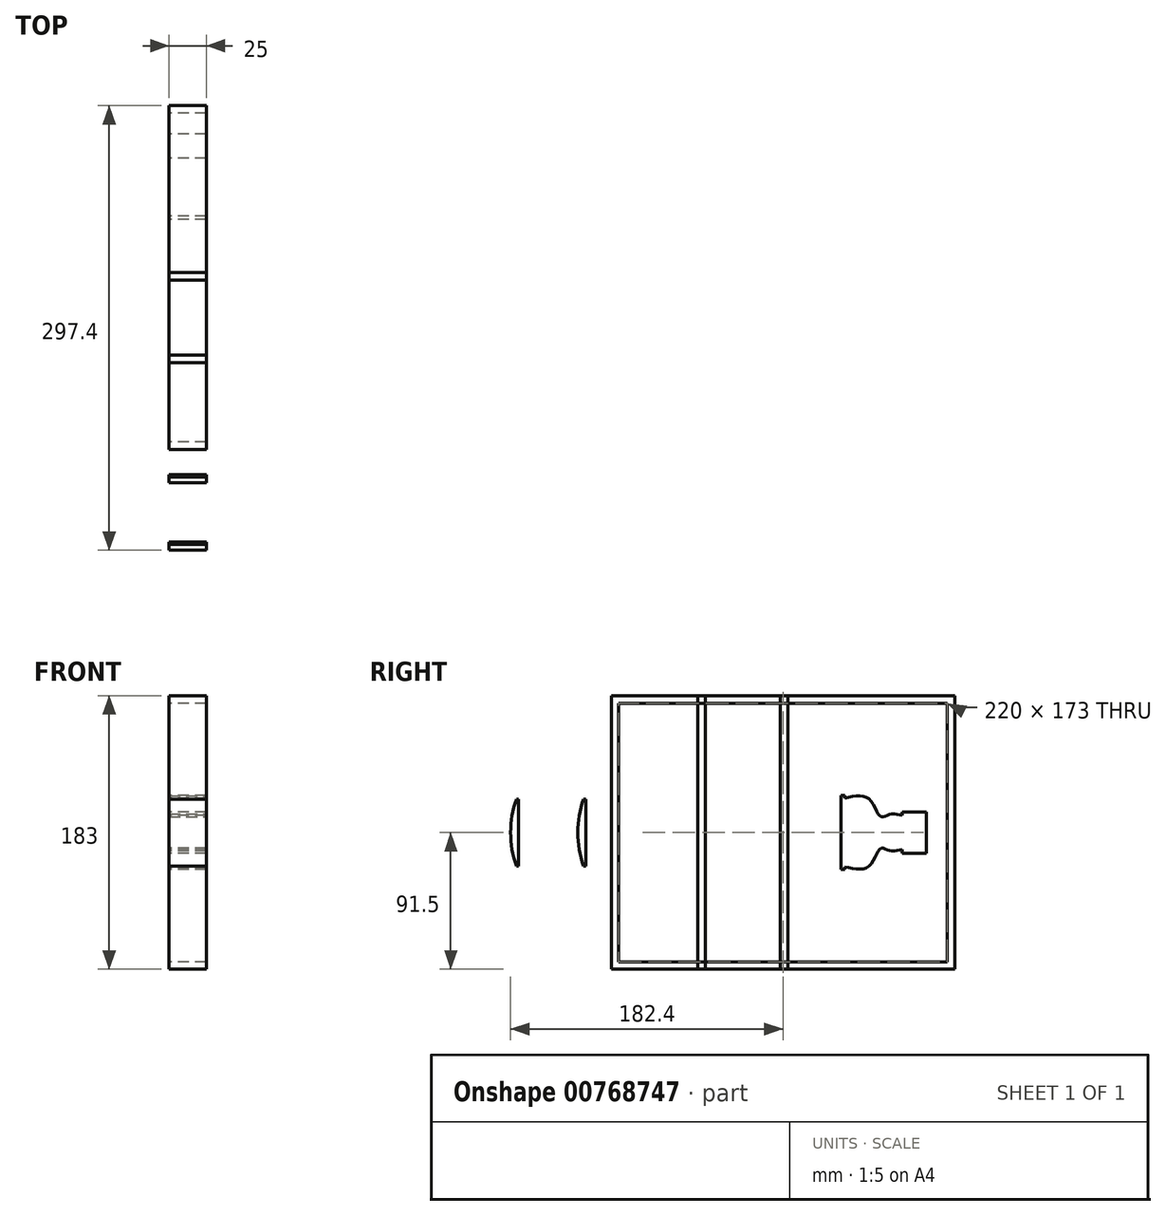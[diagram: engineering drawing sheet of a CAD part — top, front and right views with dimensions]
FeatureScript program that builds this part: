
annotation { "Feature Type Name" : "Feature", "Feature Type Description" : "" }
export const myFeature = defineFeature(function(context is Context, id is Id, definition is map)
    precondition{}
    {
        {
            var Q0;
            Q0=qCreatedBy(makeId("Right.planeOp"),FACE);
            var sketch = newSketch(context, id + "F0", { "sketchPlane" : qUnion([Q0])});
            skLineSegment(sketch, "E0", {"start": v(0, 0) * mm, "end": v(115, 0) * mm, "construction": true});
            skLineSegment(sketch, "E1.bottom", {"start": v(0, 91.5) * mm, "end": v(230, 91.5) * mm, "construction": true});
            skLineSegment(sketch, "E1.top", {"start": v(0, -91.5) * mm, "end": v(230, -91.5) * mm, "construction": true});
            skLineSegment(sketch, "E1.left", {"start": v(0, 91.5) * mm, "end": v(0, -91.5) * mm, "construction": true});
            skLineSegment(sketch, "E1.right", {"start": v(230, 91.5) * mm, "end": v(230, -91.5) * mm, "construction": true});
            skPoint(sketch, "E1.middle", {"position": v(115, 0) * mm});
            skLineSegment(sketch, "E2", {"start": v(58, 91.5) * mm, "end": v(58, -91.5) * mm, "construction": true});
            skLineSegment(sketch, "E3", {"start": v(121, -91.5) * mm, "end": v(121, 91.5) * mm, "construction": true});
            skLineSegment(sketch, "E4.0", {"start": v(65.7, 91.5) * mm, "end": v(65.7, -91.5) * mm, "construction": true});
            skLineSegment(sketch, "E5.0", {"start": v(113.3, -91.5) * mm, "end": v(113.3, 91.5) * mm, "construction": true});
            skLineSegment(sketch, "E6.bottom", {"start": v(0, 37.5) * mm, "end": v(-62, 37.5) * mm, "construction": true});
            skLineSegment(sketch, "E6.top", {"start": v(0, -37.5) * mm, "end": v(-62, -37.5) * mm, "construction": true});
            skLineSegment(sketch, "E6.right", {"start": v(-62, 37.5) * mm, "end": v(-62, -37.5) * mm, "construction": true});
            skLineSegment(sketch, "E7.0", {"start": v(11, 80.5) * mm, "end": v(219, 80.5) * mm, "construction": true});
            skLineSegment(sketch, "E7.1", {"start": v(11, 80.5) * mm, "end": v(11, -80.5) * mm, "construction": true});
            skLineSegment(sketch, "E7.2", {"start": v(11, -80.5) * mm, "end": v(219, -80.5) * mm, "construction": true});
            skLineSegment(sketch, "E7.3", {"start": v(219, 80.5) * mm, "end": v(219, -80.5) * mm, "construction": true});
            skLineSegment(sketch, "E8", {"start": v(-62, 0) * mm, "end": v(0, 0) * mm, "construction": true});
            skLineSegment(sketch, "E9", {"start": v(-17, 37.5) * mm, "end": v(-17, -37.5) * mm, "construction": true});
            skSolve(sketch);
        }
        {
            var Q0;
            Q0=qCreatedBy(makeId("Right.planeOp"),FACE);
            var sketch = newSketch(context, id + "F1", { "sketchPlane" : qUnion([Q0])});
            skLineSegment(sketch, "E10", {"start": v(153.87, 24.75) * mm, "end": v(153.87, -24.75) * mm, "construction": true});
            skLineSegment(sketch, "E11", {"start": v(0, 0) * mm, "end": v(202.87, 0) * mm, "construction": true});
            skLineSegment(sketch, "E12.bottom", {"start": v(210.87, 13.75) * mm, "end": v(194.87, 13.75) * mm, "construction": true});
            skLineSegment(sketch, "E12.top", {"start": v(210.87, -13.75) * mm, "end": v(194.87, -13.75) * mm, "construction": true});
            skLineSegment(sketch, "E12.left", {"start": v(210.87, 13.75) * mm, "end": v(210.87, -13.75) * mm, "construction": true});
            skLineSegment(sketch, "E12.right", {"start": v(194.87, 13.75) * mm, "end": v(194.87, -13.75) * mm, "construction": true});
            skPoint(sketch, "E12.middle", {"position": v(202.87, 0) * mm});
            skLineSegment(sketch, "E13.0", {"start": v(156.17, 24.75) * mm, "end": v(156.17, -24.75) * mm, "construction": true});
            skLineSegment(sketch, "E14", {"start": v(153.87, 24.75) * mm, "end": v(156.17, 24.75) * mm, "construction": true});
            skLineSegment(sketch, "E15", {"start": v(153.87, -24.75) * mm, "end": v(156.17, -24.75) * mm, "construction": true});
            skFitSpline(sketch, "E16", {"points": [v(156.17, 22.99) * mm, v(180.9, 13.2) * mm, v(194.87, 11.35) * mm], "startDerivative": vector(85.68, -3.1) * mm, "endDerivative": vector(63.31, -4.77) * mm, "construction": true});
            skFitSpline(sketch, "E17.MirrorCS", {"points": [v(156.17, -22.99) * mm, v(180.9, -13.2) * mm, v(194.87, -11.35) * mm], "startDerivative": vector(85.68, 3.1) * mm, "endDerivative": vector(63.31, 4.77) * mm, "construction": true});
            skPoint(sketch, "E18", {"position": v(156.17, 0) * mm});
            skSolve(sketch);
        }
        {
            var Q0;
            Q0=qCreatedBy(makeId("Right.planeOp"),FACE);
            var sketch = newSketch(context, id + "F2", { "sketchPlane" : qUnion([Q0])});
            skLineSegment(sketch, "E19.0", {"start": v(0, 37.5) * mm, "end": v(-62, 37.5) * mm, "construction": true});
            skLineSegment(sketch, "E19.1", {"start": v(-62, 37.5) * mm, "end": v(-62, -37.5) * mm, "construction": true});
            skLineSegment(sketch, "E19.2", {"start": v(-17, 37.5) * mm, "end": v(-17, -37.5) * mm, "construction": true});
            skLineSegment(sketch, "E19.3", {"start": v(0, -37.5) * mm, "end": v(-62, -37.5) * mm, "construction": true});
            skLineSegment(sketch, "E19.4", {"start": v(0, 91.5) * mm, "end": v(0, -91.5) * mm, "construction": true});
            skLineSegment(sketch, "E19.5", {"start": v(0, 91.5) * mm, "end": v(230, 91.5) * mm, "construction": true});
            skLineSegment(sketch, "E19.6", {"start": v(230, 91.5) * mm, "end": v(230, -91.5) * mm, "construction": true});
            skLineSegment(sketch, "E19.7", {"start": v(0, -91.5) * mm, "end": v(230, -91.5) * mm, "construction": true});
            skLineSegment(sketch, "E19.8", {"start": v(58, 91.5) * mm, "end": v(58, -91.5) * mm, "construction": true});
            skLineSegment(sketch, "E19.9", {"start": v(113.3, -91.5) * mm, "end": v(113.3, 91.5) * mm, "construction": true});
            skLineSegment(sketch, "E20.0", {"start": v(210.87, 13.75) * mm, "end": v(194.87, 13.75) * mm});
            skFitSpline(sketch, "E20.1", {"points": [v(156.17, 22.99) * mm, v(172.7, 22.39) * mm, v(180.38, 10.65) * mm, v(185.98, 12.02) * mm, v(194.87, 11.35) * mm]});
            skFitSpline(sketch, "E20.2", {"points": [v(156.17, -22.99) * mm, v(172.7, -22.39) * mm, v(180.38, -10.65) * mm, v(185.98, -12.02) * mm, v(194.87, -11.35) * mm]});
            skLineSegment(sketch, "E20.3", {"start": v(210.87, -13.75) * mm, "end": v(194.87, -13.75) * mm});
            skLineSegment(sketch, "E20.4", {"start": v(210.87, 13.75) * mm, "end": v(210.87, -13.75) * mm});
            skLineSegment(sketch, "E20.5", {"start": v(153.87, 24.75) * mm, "end": v(153.87, -24.75) * mm});
            skLineSegment(sketch, "E20.6", {"start": v(153.87, 24.75) * mm, "end": v(156.17, 24.75) * mm});
            skLineSegment(sketch, "E20.7", {"start": v(153.87, -24.75) * mm, "end": v(156.17, -24.75) * mm});
            skLineSegment(sketch, "E21", {"start": v(156.17, 22.99) * mm, "end": v(156.17, 24.75) * mm});
            skLineSegment(sketch, "E22", {"start": v(156.17, -22.99) * mm, "end": v(156.17, -24.75) * mm});
            skLineSegment(sketch, "E23", {"start": v(194.87, -13.75) * mm, "end": v(194.87, -11.35) * mm});
            skLineSegment(sketch, "E24", {"start": v(194.87, 11.35) * mm, "end": v(194.87, 13.75) * mm});
            skLineSegment(sketch, "E25.0", {"start": v(225, 86.5) * mm, "end": v(225, -86.5) * mm, "construction": true});
            skLineSegment(sketch, "E25.1", {"start": v(5, 86.5) * mm, "end": v(225, 86.5) * mm, "construction": true});
            skLineSegment(sketch, "E25.2", {"start": v(5, 86.5) * mm, "end": v(5, -86.5) * mm, "construction": true});
            skLineSegment(sketch, "E25.3", {"start": v(5, -86.5) * mm, "end": v(225, -86.5) * mm, "construction": true});
            skArc(sketch, "E26", {"start": v(-18.5, 22.37) * mm, "mid": v(-22.4, 0) * mm, "end": v(-18.5, -22.37) * mm});
            skLineSegment(sketch, "E27", {"start": v(-18.5, 22.38) * mm, "end": v(-17, 22.38) * mm});
            skLineSegment(sketch, "E28", {"start": v(-18.5, -22.38) * mm, "end": v(-17, -22.38) * mm});
            skLineSegment(sketch, "E29", {"start": v(-17, 22.38) * mm, "end": v(-17, -22.38) * mm});
            skArc(sketch, "E30.1.0.0", {"start": v(-63.5, 22.38) * mm, "mid": v(-67.4, 0) * mm, "end": v(-63.5, -22.38) * mm});
            skLineSegment(sketch, "E30.1.0.1", {"start": v(-62, 22.37) * mm, "end": v(-62, -22.37) * mm});
            skLineSegment(sketch, "E30.1.0.2", {"start": v(-63.5, -22.38) * mm, "end": v(-62, -22.38) * mm});
            skLineSegment(sketch, "E30.1.0.3", {"start": v(-63.5, 22.38) * mm, "end": v(-62, 22.38) * mm});
            skLineSegment(sketch, "E30.direction1", {"start": v(-18.5, -22.37) * mm, "end": v(-63.5, -22.37) * mm, "construction": true});
            skSolve(sketch);
        }
        {
            var Q0;
            Q0=qCreatedBy(makeId("Right.planeOp"),FACE);
            var sketch = newSketch(context, id + "F3", { "sketchPlane" : qUnion([Q0])});
            skLineSegment(sketch, "E31.0", {"start": v(5, 86.5) * mm, "end": v(5, -86.5) * mm});
            skLineSegment(sketch, "E31.1", {"start": v(0, 91.5) * mm, "end": v(0, -91.5) * mm});
            skLineSegment(sketch, "E31.2", {"start": v(5, -86.5) * mm, "end": v(225, -86.5) * mm});
            skLineSegment(sketch, "E31.3", {"start": v(0, -91.5) * mm, "end": v(230, -91.5) * mm});
            skLineSegment(sketch, "E31.4", {"start": v(5, 86.5) * mm, "end": v(225, 86.5) * mm});
            skLineSegment(sketch, "E31.5", {"start": v(0, 91.5) * mm, "end": v(230, 91.5) * mm});
            skLineSegment(sketch, "E31.6", {"start": v(225, 86.5) * mm, "end": v(225, -86.5) * mm});
            skLineSegment(sketch, "E31.7", {"start": v(230, 91.5) * mm, "end": v(230, -91.5) * mm});
            skSolve(sketch);
        }
        {
            var Q0;
            Q0 = qSketchRegion(id + "F3", true);
            extrude(context, id + "F4", {"entities" : qUnion([Q0]), "depth" : 25 * mm, "offsetDistance" : 25 * mm});
        }
        {
            var Q0;
            Q0 = qSketchRegion(id + "F2", true);
            extrude(context, id + "F5", {"entities" : qUnion([Q0]), "depth" : 25 * mm, "offsetDistance" : 25 * mm});
        }
        {
            var Q0;
            Q0=qCreatedBy(makeId("Right.planeOp"),FACE);
            var sketch = newSketch(context, id + "F6", { "sketchPlane" : qUnion([Q0])});
            skLineSegment(sketch, "E32.bottom", {"start": v(58, 91.5) * mm, "end": v(63, 91.5) * mm});
            skLineSegment(sketch, "E32.top", {"start": v(58, -91.5) * mm, "end": v(63, -91.5) * mm});
            skLineSegment(sketch, "E32.left", {"start": v(58, 91.5) * mm, "end": v(58, -91.5) * mm});
            skLineSegment(sketch, "E32.right", {"start": v(63, 91.5) * mm, "end": v(63, -91.5) * mm});
            skLineSegment(sketch, "E33.bottom", {"start": v(113.3, 91.5) * mm, "end": v(118.3, 91.5) * mm});
            skLineSegment(sketch, "E33.top", {"start": v(113.3, -91.5) * mm, "end": v(118.3, -91.5) * mm});
            skLineSegment(sketch, "E33.left", {"start": v(113.3, 91.5) * mm, "end": v(113.3, -91.5) * mm});
            skLineSegment(sketch, "E33.right", {"start": v(118.3, 91.5) * mm, "end": v(118.3, -91.5) * mm});
            skSolve(sketch);
        }
        {
            var Q0;
            Q0 = qSketchRegion(id + "F6", true);
            extrude(context, id + "F7", {"entities" : qUnion([Q0]), "depth" : 25 * mm, "offsetDistance" : 25 * mm});
        }
    });
